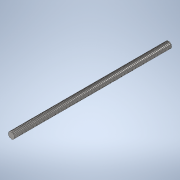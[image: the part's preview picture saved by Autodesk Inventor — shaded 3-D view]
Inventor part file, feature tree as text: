
AUTODESK INVENTOR PART (.ipt)
format: ipt  version: 2020 (Build 240168000, 168)  size: 960,512 bytes
history: native  units: mm
features: sketch x2, extrude x1, helix x1, pattern_circular x1
ambient origin geometry x8: Origin, YZ Plane, XZ Plane, XY Plane, X Axis, Y Axis, Z Axis, Center Point
bodies: Solid1 (feature_tree)
feature tree (5):
  extrude  "Extrusion1"  Depth=8.0mm TaperAngle=0.0deg
  helix  "Coil1"  [1 undecoded]
  pattern_circular  "Circular Pattern1"  Count=4 Angle=360.0deg
  sketch  "Sketch1"  dims[d0=8.0mm d1=200.0mm d2=0.0mm d3=1.0mm]
  sketch  "Sketch2"  dims[d4=3.8mm d5=8.0mm d6=10.0mm d7=250.0mm d8=0.0mm d9=90.0deg d10=90.0deg d11=0.0mm d12=0.0mm d13=40.0mm d14=360.0deg]
note: 1 required parameter value undecoded (feature->parameter linkage not recoverable at this tier; creation-order binding heuristic only, values carry confidence <= 0.55)
